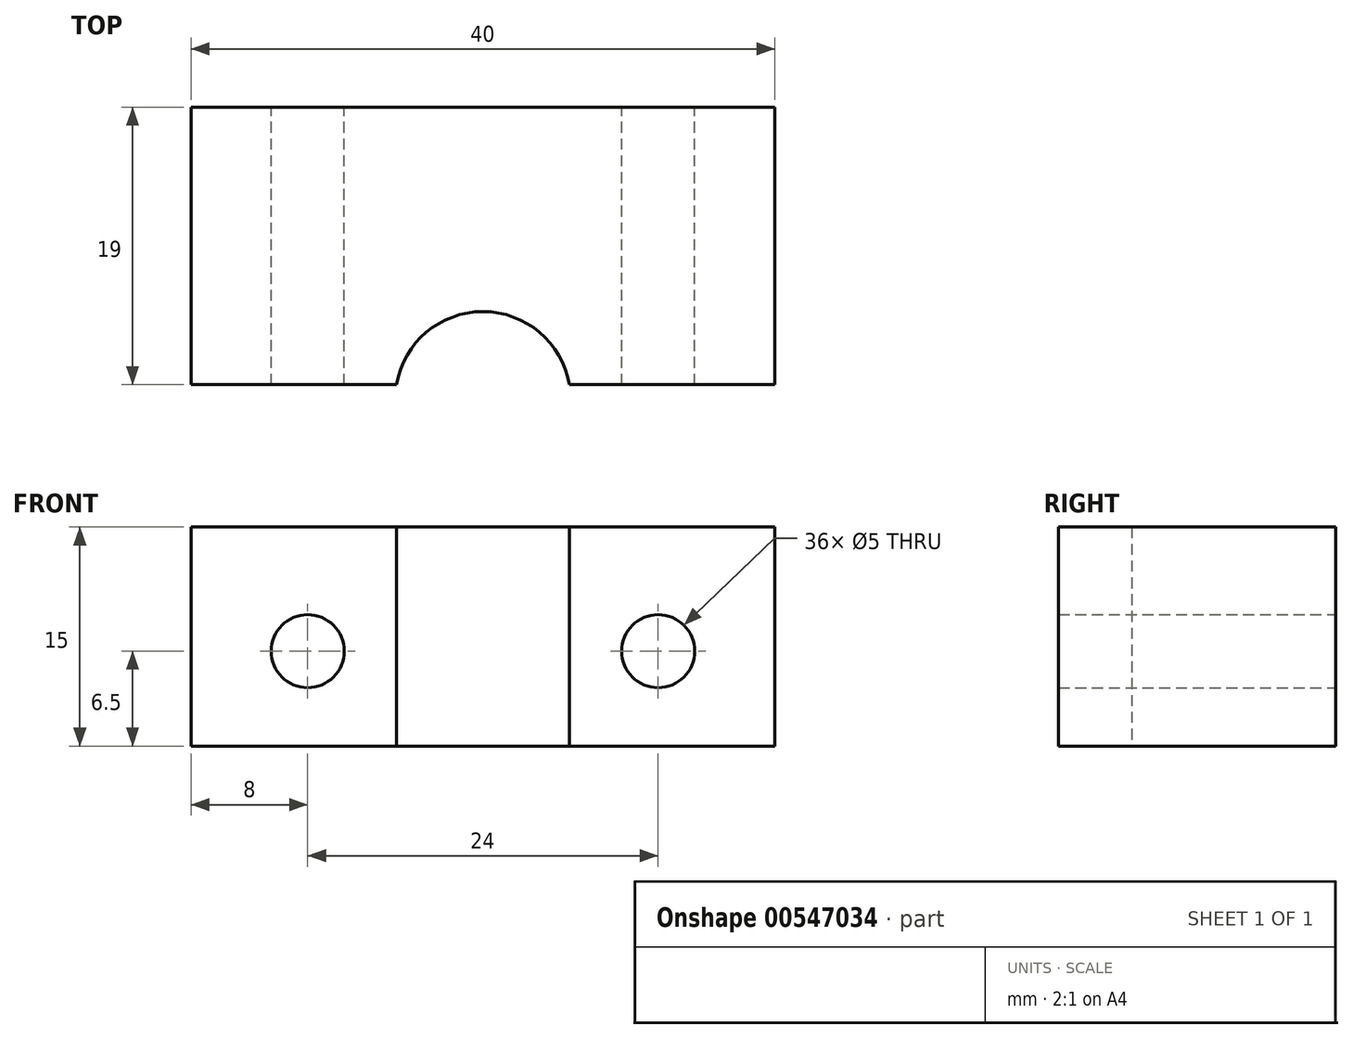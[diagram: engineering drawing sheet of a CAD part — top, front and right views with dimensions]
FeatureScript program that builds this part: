
annotation { "Feature Type Name" : "Feature", "Feature Type Description" : "" }
export const myFeature = defineFeature(function(context is Context, id is Id, definition is map)
    precondition{}
    {
        {
            var Q0;
            Q0=qCreatedBy(makeId("Top.planeOp"),FACE);
            var sketch = newSketch(context, id + "F0", { "sketchPlane" : qUnion([Q0])});
            skLineSegment(sketch, "E0.bottom", {"start": v(0, 0) * mm, "end": v(40, 0) * mm});
            skLineSegment(sketch, "E0.top", {"start": v(0, -19) * mm, "end": v(40, -19) * mm});
            skLineSegment(sketch, "E0.left", {"start": v(0, 0) * mm, "end": v(0, -19) * mm});
            skLineSegment(sketch, "E0.right", {"start": v(40, 0) * mm, "end": v(40, -19) * mm});
            skCircle(sketch, "E1", {"center": v(20, -20) * mm, "radius": 6 * mm});
            skSolve(sketch);
        }
        {
            var Q0;
            Q0=makeQuery(id+"F0.imprint","IMPRINT",FACE,{"disambiguationData":[TD([[makeQuery(id+"F0.imprint","IMPRINT",EDGE,{"derivedFrom":sQuery(id+"F0.wireOp",EDGE,"E0.bottom")}),-1.0]])]});
            extrude(context, id + "F1", {"entities" : qUnion([Q0]), "depth" : 15 * mm, "offsetDistance" : 25 * mm});
        }
        {
            var Q0;
            Q0=makeQuery(id+"F1.opExtrude","SWEPT_FACE",FACE,{"disambiguationData":[OSD([sQuery(id+"F0.wireOp",EDGE,"E0.bottom")])]});
            var sketch = newSketch(context, id + "F2", { "sketchPlane" : qUnion([Q0])});
            skPoint(sketch, "E2", {"position": v(-8, 6.5) * mm});
            skPoint(sketch, "E3", {"position": v(-32, 6.5) * mm});
            skSolve(sketch);
        }
        {
            var Q0;
            Q0=sQuery(id+"F2.wireOp",VERTEX,"E2");
            var Q1;
            Q1=sQuery(id+"F2.wireOp",VERTEX,"E3");
            var Q2;
            Q2=makeQuery(id+"F1.opExtrude","SWEPT_BODY",BODY,{"disambiguationData":[OSD([sQuery(id+"F0.wireOp",EDGE,"E0.bottom"),sQuery(id+"F0.wireOp",EDGE,"E0.top"),sQuery(id+"F0.wireOp",EDGE,"E0.left"),sQuery(id+"F0.wireOp",EDGE,"E0.right"),sQuery(id+"F0.wireOp",EDGE,"E1")])]});
            hole(context, id + "F3", {"style" : HoleStyle.SIMPLE, "endStyle" : HoleEndStyle.THROUGH, "holeDiameter" : 5 * mm, "isTappedThrough" : true, "tappedDepth" : 12 * mm, "tapClearance" : 3, "startFromSketch" : true, "locations" : qUnion([Q0, Q1]), "scope" : qUnion([Q2])});
        }
    });
